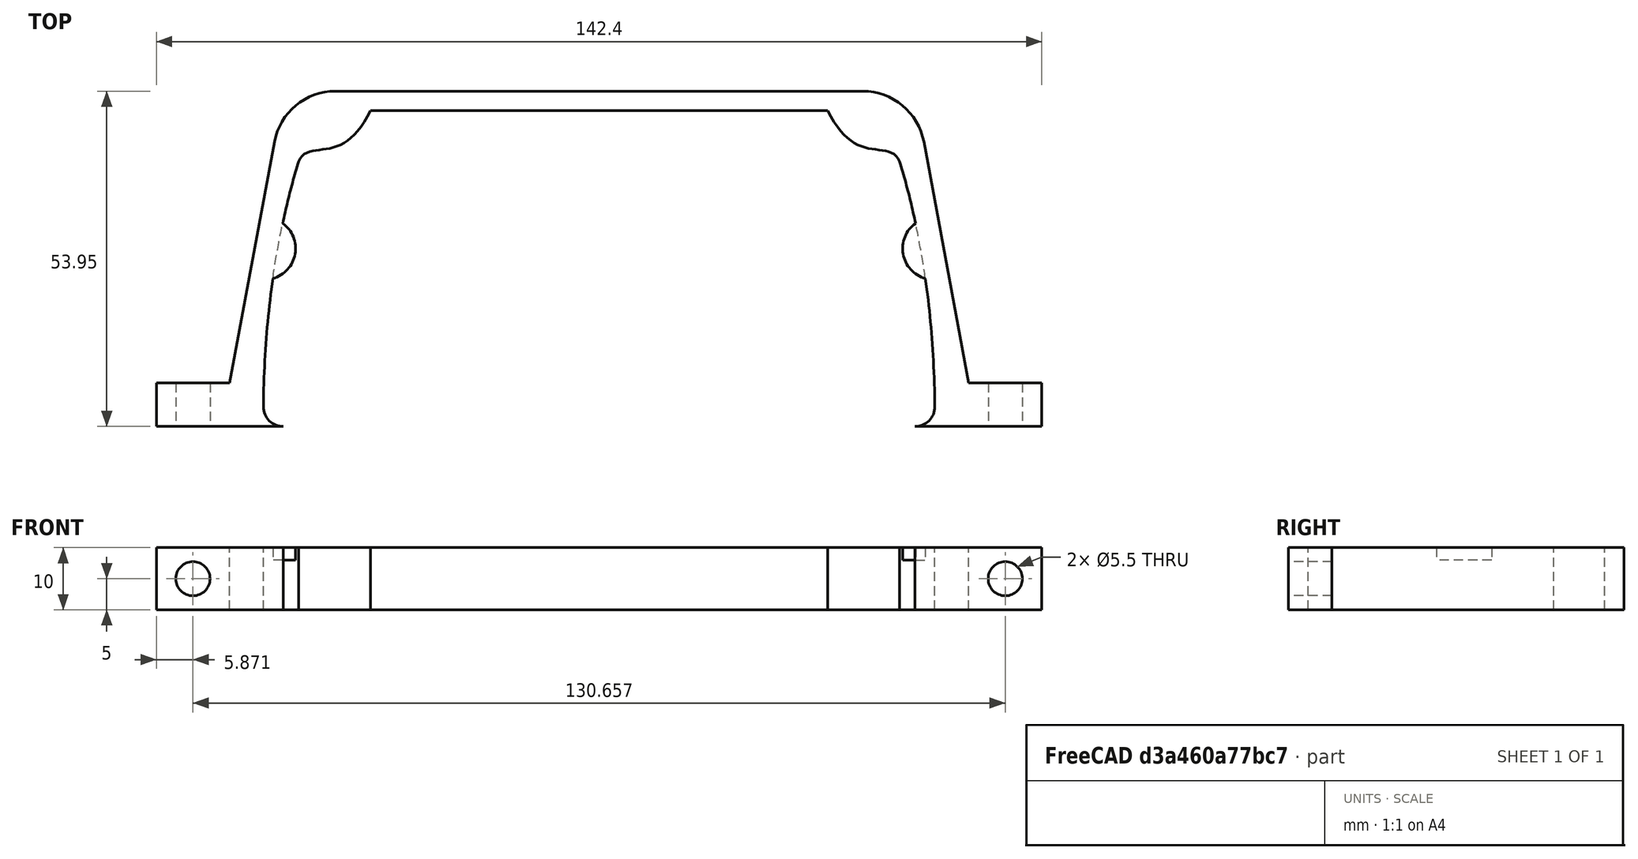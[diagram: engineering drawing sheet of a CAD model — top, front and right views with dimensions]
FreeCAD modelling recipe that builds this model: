
FCSTD DOCUMENT  (FreeCAD 0.19R24415 (Git))
Label: 220V_inverter_holder
License: All rights reserved
LicenseURL: http://en.wikipedia.org/wiki/All_rights_reserved
objects: Sketcher::SketchObject×4, PartDesign::Mirrored×4, PartDesign::Pad×2, PartDesign::Body×2, PartDesign::Hole×1, Image::ImagePlane×1, PartDesign::Fillet×1, App::Part×1, Part::Cut×1, PartDesign::Pocket×1
note: 21 computed .brp shape members not serialized (recipe doc carries the construction recipe); baked Part::Feature solids carry a one-line shape summary decoded from their .brp

FEATURE [Sketcher::SketchObject] Sketch
  FullyConstrained = true
  MapMode = 5
  Support = -> [XY_Plane]
  expr: Constraints[51] = 43.18 * .Constraints.unity
  expr: Constraints[49] = 39.79 * .Constraints.unity
  expr: Constraints[45] = 37.27 * .Constraints.unity
  expr: Constraints[47] = 37.97 * .Constraints.unity
  expr: Constraints[44] = 36.49 * .Constraints.unity
  expr: Constraints[48] = 32.87 * .Constraints.unity
  expr: Constraints[46] = 40.36 * .Constraints.unity
  expr: Constraints[42] = 41.06 * .Constraints.unity
  expr: Constraints[43] = 36.24 * .Constraints.unity
  expr: Constraints[38] = 21.03 * .Constraints.unity
  expr: Constraints[37] = 45.68 * .Constraints.unity
  expr: Constraints[50] = 31.25 * .Constraints.unity
  expr: .Constraints.unity = .Constraints.width / 91.75
  sketch-geometry (21):
    g0: LineSegment StartX=-54 StartY=3.17232 StartZ=0 EndX=54 EndY=3.17232 EndZ=0
    g1: ArcOfCircle CenterX=50.8277 CenterY=3.17232 CenterZ=0 NormalX=0 NormalY=0 NormalZ=1 AngleXU=0 Radius=3.17232 StartAngle=4.71239 EndAngle=6.28319
    g2: Circle CenterX=54 CenterY=3.17232 CenterZ=0 NormalX=0 NormalY=0 NormalZ=1 AngleXU=0 Radius=1
    g3: Circle CenterX=53.7705 CenterY=24.7547 CenterZ=0 NormalX=0 NormalY=0 NormalZ=1 AngleXU=0 Radius=1
    g4: Circle CenterX=48.3322 CenterY=42.6585 CenterZ=0 NormalX=0 NormalY=0 NormalZ=1 AngleXU=0 Radius=1
    g5: BSplineCurve PolesCount=3 KnotsCount=2 Degree=2 IsPeriodic=0
    g6: GeomPoint X=54 Y=3.17232 Z=0
    g7: GeomPoint X=48.3322 Y=42.6585 Z=0
    g8-g12: Circle x5 (B-spline internal-alignment scaffolding for g13; pole/knot coordinates omitted)
    g13: BSplineCurve PolesCount=5 KnotsCount=3 Degree=3 IsPeriodic=0
    g14: GeomPoint X=48.3322 Y=42.6585 Z=0
    g15: GeomPoint X=43.0264 Y=44.8185 Z=0
    g16: GeomPoint X=36.7847 Y=50.8277 Z=0
    g17: LineSegment StartX=36.7847 StartY=50.8277 StartZ=0 EndX=0 EndY=50.8277 EndZ=0
    g18: LineSegment StartX=50.8277 StartY=0 StartZ=0 EndX=0 EndY=0 EndZ=0
    g19: LineSegment StartX=0 StartY=50.8277 StartZ=0 EndX=0 EndY=0 EndZ=0
    g20: LineSegment StartX=0 StartY=0 StartZ=0 EndX=-1.17711 EndY=0 EndZ=0
  constraints (45):
    c: Symmetric(g0,g0,g-2)
    c: Coincident(g5,g1)
    c: Weight(g2) = 1
    c: Equal(g2,g3)
    c: Equal(g2,g4)
    c: InternalAlignment(g2,g5)
    c: InternalAlignment(g3,g5)
    c: InternalAlignment(g4,g5)
    c: InternalAlignment(g6,g5)
    c: InternalAlignment(g7,g5)
    c: Coincident(g13,g5)
    c: Weight(g8) = 1
    c: Equal(g8, g9-g12) x4
    c: InternalAlignment(g8-g12 -> g13) x5
    c: InternalAlignment(g14,g13)
    c: InternalAlignment(g15,g13)
    c: InternalAlignment(g16,g13)
    c: Coincident(g17,g13)
    c: Coincident(g18,g-1)
    c: Horizontal(g18)
    c: Coincident(g19,g17)
    c: Coincident(g19,g18)
    c: Vertical(g19)
    c: Horizontal(g17)
    c: Coincident(g1,g18)
    c: Coincident(g0,g1)
    c: Horizontal(g1,g1)
    c: DistanceX(g0,g0) = 108  'width'
    c: Vertical(g1,g1)
    c: Equal(g18,g19)
    c: DistanceX(g3) = 53.7705
    c: DistanceY(g3) = 24.7547
    c: Coincident(g20,g18)
    c: Horizontal(g20)
    c: DistanceX(g20,g20) = 1.17711  'unity'
    c: DistanceX(g5) = 48.3322
    c: DistanceY(g5) = 42.6585
    c: DistanceX(g18,g10) = 42.9528
    c: DistanceY(g18,g10) = 43.871
    c: DistanceX(g18,g9) = 47.5082
    c: DistanceY(g18,g9) = 44.6949
    c: DistanceX(g18,g11) = 38.6917
    c: DistanceY(g18,g11) = 46.8373
    c: DistanceX(g18,g13) = 36.7847
    c: DistanceY(g18,g13) = 50.8277
FEATURE [PartDesign::Pad] Pad
  Direction = (1,1,1)
  Length = 10
  Length2 = 100
  Profile = -> Sketch
  Type = 0
FEATURE [Sketcher::SketchObject] Sketch001
  FullyConstrained = false
  MapMode = 5
  Support = -> [XY_Plane002]
  sketch-geometry (6):
    g0: LineSegment StartX=0 StartY=0 StartZ=0 EndX=71.1998 EndY=0 EndZ=0
    g1: LineSegment StartX=71.1998 StartY=0 StartZ=0 EndX=71.1998 EndY=6.98564 EndZ=0
    g2: LineSegment StartX=71.1998 StartY=6.98564 StartZ=0 EndX=59.4577 EndY=6.98564 EndZ=0
    g3: LineSegment StartX=59.4577 StartY=6.98564 StartZ=0 EndX=50.7044 EndY=53.9542 EndZ=0
    g4: LineSegment StartX=50.7044 StartY=53.9542 StartZ=0 EndX=0 EndY=53.9542 EndZ=0
    g5: LineSegment StartX=0 StartY=53.9542 StartZ=0 EndX=0 EndY=0 EndZ=0
  constraints (12):
    c: Coincident(g0,g-1)
    c: PointOnObject(g0,g-1)
    c: Coincident(g1,g0)
    c: Vertical(g1)
    c: Coincident(g2,g1)
    c: Horizontal(g2)
    c: Coincident(g3,g2)
    c: Coincident(g4,g3)
    c: PointOnObject(g4,g-2)
    c: Horizontal(g4)
    c: Coincident(g5,g4)
    c: Coincident(g5,g0)
FEATURE [PartDesign::Pad] Pad001
  Direction = (1,1,1)
  Length = 10
  Length2 = 100
  Profile = -> Sketch001
  Type = 0
FEATURE [Sketcher::SketchObject] Sketch002
  ExternalGeometry = -> [Pad001]
  FullyConstrained = false
  MapMode = 5
  Placement = pos=(0,6.98564,0) rot=(0,0.707107,0.707107;3.14159rad)
  Support = -> [Pad001]
  sketch-geometry (1):
    g0: Circle CenterX=-65.3287 CenterY=5 CenterZ=0 NormalX=0 NormalY=0 NormalZ=1 AngleXU=0 Radius=2.16034
  constraints (1):
    c: Symmetric(g-4,g-3,g0)
FEATURE [PartDesign::Hole] Hole
  BaseFeature = -> Pad001
  Depth = 25
  DepthType = 1
  Diameter = 5.5
  DrillForDepth = false
  DrillPoint = 1
  DrillPointAngle = 118
  HoleCutCountersinkAngle = 90
  HoleCutCustomValues = false
  HoleCutDepth = 0
  HoleCutDiameter = 6.1
  HoleCutType = 0
  ModelActualThread = false
  Profile = -> Sketch002
  Tapered = false
  TaperedAngle = 90
  ThreadAngle = 0
  ThreadClass = 0
  ThreadCutOffInner = 0
  ThreadCutOffOuter = 0
  ThreadDirection = 0
  ThreadFit = 0
  ThreadPitch = 0
  ThreadSize = 13
  ThreadType = 1
  Threaded = false
FEATURE [PartDesign::Mirrored] Mirrored
  BaseFeature = -> Pad
  MirrorPlane = -> Sketch [V_Axis]
  Originals = -> [Pad]
FEATURE [PartDesign::Mirrored] Mirrored001
  BaseFeature = -> Hole
  MirrorPlane = -> Sketch001 [V_Axis]
  Originals = -> [Pad001]
FEATURE [PartDesign::Mirrored] Mirrored002
  BaseFeature = -> Mirrored001
  MirrorPlane = -> Sketch002 [V_Axis]
  Originals = -> [Hole]
FEATURE [Image::ImagePlane] ImagePlane002
  Placement = pos=(1,26.3,0) rot=(0,0,1;0rad)
  XSize = 127.928
  YSize = 77.4612
FEATURE [PartDesign::Fillet] Fillet
  Base = -> Mirrored002 [Edge35,Edge38]
  BaseFeature = -> Mirrored002
  Radius = 10
  SupportTransform = false
FEATURE [PartDesign::Body] Body001
  Group = -> [Sketch001,Pad001,Sketch002,Hole,Mirrored001,Mirrored002,Fillet]
  Origin = -> Origin002
  Tip = -> Fillet
FEATURE [PartDesign::Body] Body
  Group = -> [Sketch,Pad,Mirrored,Sketch003,Pocket,Mirrored003]
  Origin = -> Origin
  Tip = -> Mirrored003
FEATURE [App::Part] Part
  Group = -> [Body,Body001,Cut]
  Origin = -> Origin001
FEATURE [Part::Cut] Cut
  Base = -> Body001
  Tool = -> Body
FEATURE [Sketcher::SketchObject] Sketch003
  FullyConstrained = true
  MapMode = 5
  Placement = pos=(0,0,10) rot=(0,0,1;0rad)
  Support = -> [Cut]
  sketch-geometry (2):
    g0: ArcOfCircle CenterX=53.8122 CenterY=28.6236 CenterZ=0 NormalX=0 NormalY=0 NormalZ=1 AngleXU=0 Radius=5 StartAngle=1.5708 EndAngle=4.71239
    g1: LineSegment StartX=53.8122 StartY=23.6236 StartZ=0 EndX=53.8122 EndY=33.6236 EndZ=0
  constraints (7):
    c: Vertical(g0,g0)
    c: Vertical(g0,g0)
    c: DistanceY(g0,g0) = 10
    c: DistanceX(g0) = 53.8122
    c: DistanceY(g0) = 28.6236
    c: Coincident(g1,g0)
    c: Coincident(g1,g0)
FEATURE [PartDesign::Pocket] Pocket
  BaseFeature = -> Mirrored
  Length = 2
  Length2 = 100
  Profile = -> Sketch003
  Type = 0
FEATURE [PartDesign::Mirrored] Mirrored003
  BaseFeature = -> Pocket
  MirrorPlane = -> Sketch003 [V_Axis]
  Originals = -> [Pocket]
